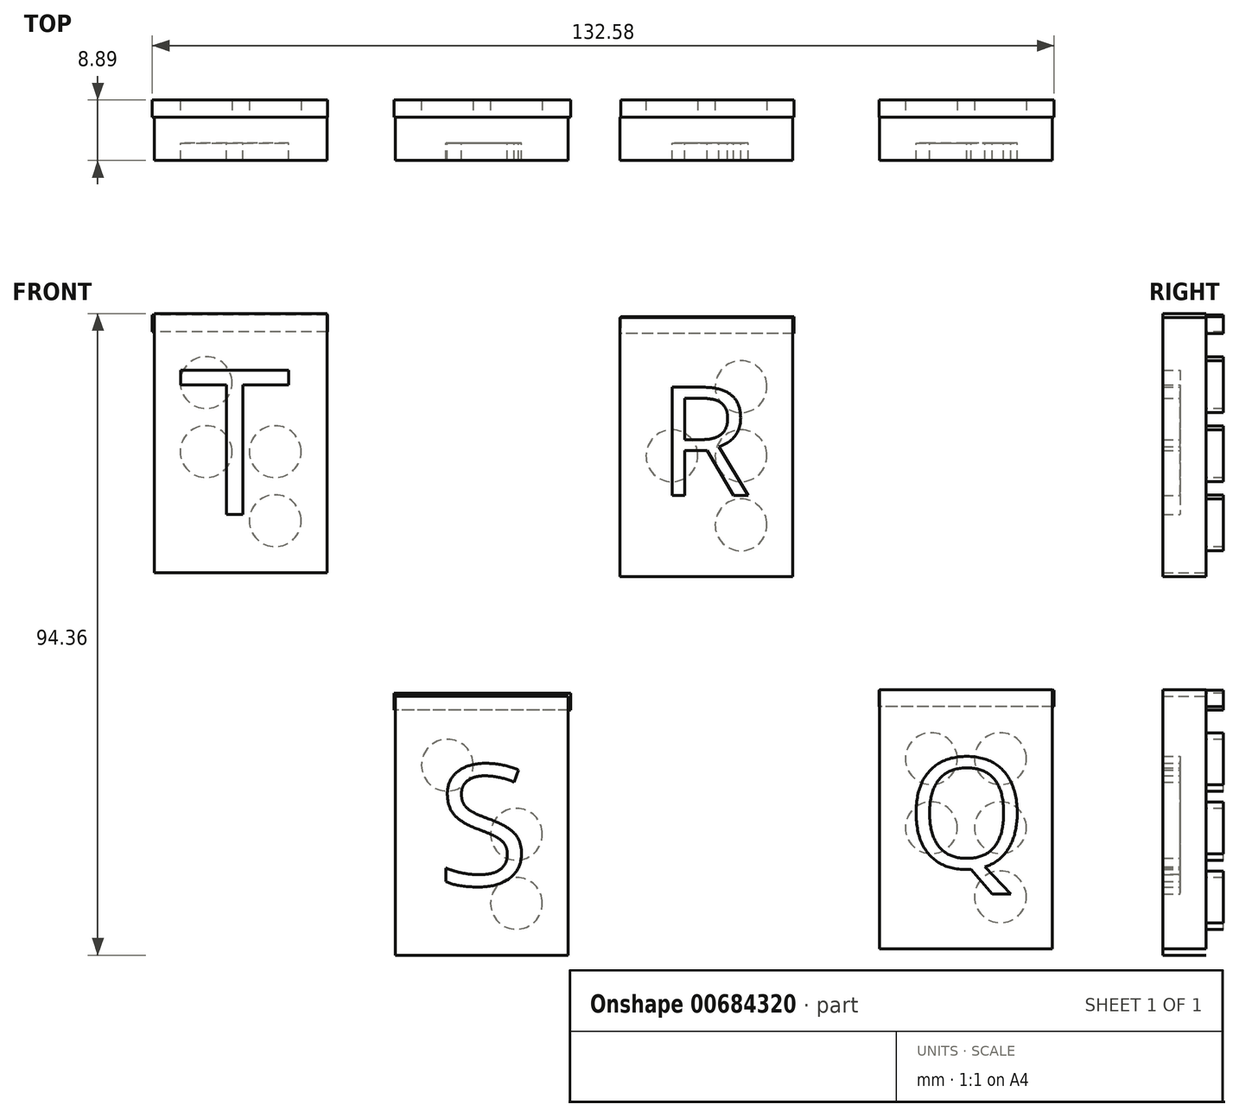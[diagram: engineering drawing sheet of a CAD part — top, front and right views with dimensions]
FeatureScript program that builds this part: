
annotation { "Feature Type Name" : "Feature", "Feature Type Description" : "" }
export const myFeature = defineFeature(function(context is Context, id is Id, definition is map)
    precondition{}
    {
        {
            var Q0;
            Q0=qCreatedBy(makeId("Front.planeOp"),FACE);
            var sketch = newSketch(context, id + "F0", { "sketchPlane" : qUnion([Q0])});
            skLineSegment(sketch, "E0.bottom", {"start": v(-58.76, 38.35) * mm, "end": v(-33.36, 38.35) * mm});
            skLineSegment(sketch, "E0.top", {"start": v(-58.76, 0.25) * mm, "end": v(-33.36, 0.25) * mm});
            skLineSegment(sketch, "E0.left", {"start": v(-58.76, 38.35) * mm, "end": v(-58.76, 0.25) * mm});
            skLineSegment(sketch, "E0.right", {"start": v(-33.36, 38.35) * mm, "end": v(-33.36, 0.25) * mm});
            skLineSegment(sketch, "E1.bottom", {"start": v(-23.3, -17.91) * mm, "end": v(2.1, -17.91) * mm});
            skLineSegment(sketch, "E1.top", {"start": v(-23.3, -56.01) * mm, "end": v(2.1, -56.01) * mm});
            skLineSegment(sketch, "E1.left", {"start": v(-23.3, -17.91) * mm, "end": v(-23.3, -56.01) * mm});
            skLineSegment(sketch, "E1.right", {"start": v(2.1, -17.91) * mm, "end": v(2.1, -56.01) * mm});
            skLineSegment(sketch, "E2.bottom", {"start": v(47.85, -16.96) * mm, "end": v(73.25, -16.96) * mm});
            skLineSegment(sketch, "E2.top", {"start": v(47.85, -55.06) * mm, "end": v(73.25, -55.06) * mm});
            skLineSegment(sketch, "E2.left", {"start": v(47.85, -16.96) * mm, "end": v(47.85, -55.06) * mm});
            skLineSegment(sketch, "E2.right", {"start": v(73.25, -16.96) * mm, "end": v(73.25, -55.06) * mm});
            skLineSegment(sketch, "E3.bottom", {"start": v(9.7, 37.75) * mm, "end": v(35.1, 37.75) * mm});
            skLineSegment(sketch, "E3.top", {"start": v(9.7, -0.35) * mm, "end": v(35.1, -0.35) * mm});
            skLineSegment(sketch, "E3.left", {"start": v(9.7, 37.75) * mm, "end": v(9.7, -0.35) * mm});
            skLineSegment(sketch, "E3.right", {"start": v(35.1, 37.75) * mm, "end": v(35.1, -0.35) * mm});
            skSolve(sketch);
        }
        {
            var Q0;
            Q0=qSketchRegion(id+"F0",true);
            extrude(context, id + "F1", {"entities" : qUnion([Q0]), "depth" : 6.35 * mm});
        }
        {
            var Q0;
            Q0=qCreatedBy(makeId("Front.planeOp"),FACE);
            var sketch = newSketch(context, id + "F2", { "sketchPlane" : qUnion([Q0])});
            skCircle(sketch, "E4", {"center": v(27.49, 7.27) * mm, "radius": 3.81 * mm});
            skCircle(sketch, "E5", {"center": v(27.49, 17.43) * mm, "radius": 3.81 * mm});
            skCircle(sketch, "E6", {"center": v(65.63, -27.12) * mm, "radius": 3.81 * mm});
            skCircle(sketch, "E7", {"center": v(65.63, -47.44) * mm, "radius": 3.81 * mm});
            skCircle(sketch, "E8", {"center": v(-5.52, -38.23) * mm, "radius": 3.81 * mm});
            skCircle(sketch, "E9", {"center": v(-15.68, -28.07) * mm, "radius": 3.81 * mm});
            skCircle(sketch, "E10", {"center": v(27.49, 27.59) * mm, "radius": 3.81 * mm});
            skCircle(sketch, "E11", {"center": v(17.33, 17.43) * mm, "radius": 3.81 * mm});
            skCircle(sketch, "E12", {"center": v(-5.52, -48.4) * mm, "radius": 3.8 * mm});
            skCircle(sketch, "E13", {"center": v(-40.98, 18.03) * mm, "radius": 3.81 * mm});
            skCircle(sketch, "E14", {"center": v(-51.14, 28.19) * mm, "radius": 3.81 * mm});
            skCircle(sketch, "E15", {"center": v(-51.14, 18.03) * mm, "radius": 3.81 * mm});
            skCircle(sketch, "E16", {"center": v(-40.98, 7.87) * mm, "radius": 3.81 * mm});
            skCircle(sketch, "E17", {"center": v(55.47, -37.28) * mm, "radius": 3.81 * mm});
            skCircle(sketch, "E18", {"center": v(55.47, -27.12) * mm, "radius": 3.81 * mm});
            skCircle(sketch, "E19", {"center": v(65.63, -37.28) * mm, "radius": 3.81 * mm});
            skSolve(sketch);
        }
        {
            var Q0;
            Q0=qSketchRegion(id+"F2",true);
            extrude(context, id + "F3", {"entities" : qUnion([Q0]), "operationType" : NewBodyOperationType.ADD, "oppositeDirection" : true, "depth" : 2.54 * mm});
        }
        {
            var Q0;
            Q0=qCreatedBy(makeId("Front.planeOp"),FACE);
            cPlane(context, id + "F4", {"entities" : qUnion([Q0]), "cplaneType" : CPlaneType.OFFSET, "offset" : 3.8 * mm, "width" : 152.4 * mm, "height" : 152.4 * mm});
        }
        {
            var Q0;
            Q0=qCreatedBy(id+"F4.planeOp",FACE);
            var sketch = newSketch(context, id + "F5", { "sketchPlane" : qUnion([Q0])});
            skText(sketch, "E20", { "text": "Q", "fontName": "OpenSans-Regular.ttf"});
            skText(sketch, "E21", { "text": "R", "fontName": "OpenSans-Regular.ttf"});
            skText(sketch, "E22", { "text": "S", "fontName": "OpenSans-Regular.ttf"});
            skText(sketch, "E23", { "text": "T", "fontName": "OpenSans-Regular.ttf"});
            const initialGuessF5  = {"E20": [0.05185, -0.0432, 1, 0, 0.0163], "E21": [0.01516, 0.0116, 1, 0, 0.01605], "E22": [-0.0172, -0.04574, 1, 0, 0.01784], "E23": [-0.05517, 0.0088, 1, 0, 0.0214]};
            skSetInitialGuess(sketch, initialGuessF5);
            skSolve(sketch);
        }
        {
            var Q0;
            Q0=qSketchRegion(id+"F5",true);
            extrude(context, id + "F6", {"entities" : qUnion([Q0]), "operationType" : NewBodyOperationType.REMOVE, "depth" : 25.4 * mm});
        }
        {
            var Q0;
            Q0=qCreatedBy(makeId("Front.planeOp"),FACE);
            var sketch = newSketch(context, id + "F7", { "sketchPlane" : qUnion([Q0])});
            skLineSegment(sketch, "E24.bottom", {"start": v(73.52, -17.03) * mm, "end": v(47.79, -17.03) * mm});
            skLineSegment(sketch, "E24.top", {"start": v(73.52, -19.48) * mm, "end": v(47.79, -19.48) * mm});
            skLineSegment(sketch, "E24.left", {"start": v(73.52, -17.03) * mm, "end": v(73.52, -19.48) * mm});
            skLineSegment(sketch, "E24.right", {"start": v(47.79, -17.03) * mm, "end": v(47.79, -19.48) * mm});
            skLineSegment(sketch, "E25.bottom", {"start": v(35.29, 37.86) * mm, "end": v(9.8, 37.86) * mm});
            skLineSegment(sketch, "E25.top", {"start": v(35.29, 35.41) * mm, "end": v(9.8, 35.41) * mm});
            skLineSegment(sketch, "E25.left", {"start": v(35.29, 37.86) * mm, "end": v(35.29, 35.41) * mm});
            skLineSegment(sketch, "E25.right", {"start": v(9.8, 37.86) * mm, "end": v(9.8, 35.41) * mm});
            skLineSegment(sketch, "E26.bottom", {"start": v(-33.33, 38.1) * mm, "end": v(-59.06, 38.1) * mm});
            skLineSegment(sketch, "E26.top", {"start": v(-33.33, 35.66) * mm, "end": v(-59.06, 35.66) * mm});
            skLineSegment(sketch, "E26.left", {"start": v(-33.33, 38.1) * mm, "end": v(-33.33, 35.66) * mm});
            skLineSegment(sketch, "E26.right", {"start": v(-59.06, 38.1) * mm, "end": v(-59.06, 35.66) * mm});
            skLineSegment(sketch, "E27.bottom", {"start": v(2.45, -17.52) * mm, "end": v(-23.53, -17.52) * mm});
            skLineSegment(sketch, "E27.top", {"start": v(2.45, -19.97) * mm, "end": v(-23.53, -19.97) * mm});
            skLineSegment(sketch, "E27.left", {"start": v(2.45, -17.52) * mm, "end": v(2.45, -19.97) * mm});
            skLineSegment(sketch, "E27.right", {"start": v(-23.53, -17.52) * mm, "end": v(-23.53, -19.97) * mm});
            skSolve(sketch);
        }
        {
            var Q0;
            Q0=qSketchRegion(id+"F7",true);
            extrude(context, id + "F8", {"entities" : qUnion([Q0]), "operationType" : NewBodyOperationType.ADD, "oppositeDirection" : true, "depth" : 2.54 * mm});
        }
    });
